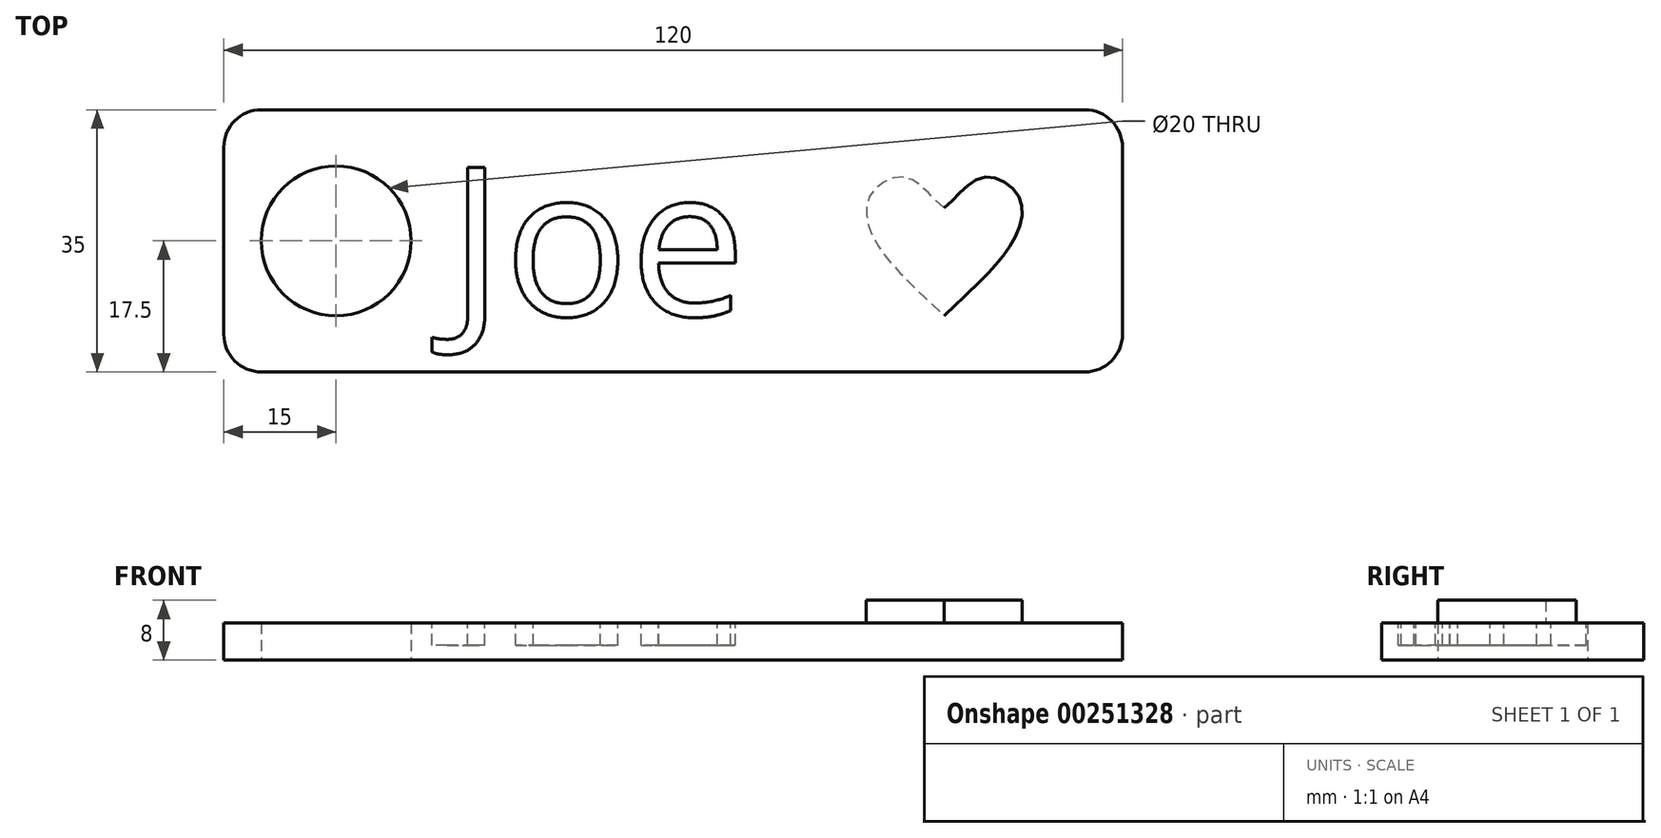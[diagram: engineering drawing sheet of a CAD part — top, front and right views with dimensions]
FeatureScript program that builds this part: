
annotation { "Feature Type Name" : "Feature", "Feature Type Description" : "" }
export const myFeature = defineFeature(function(context is Context, id is Id, definition is map)
    precondition{}
    {
        {
            var Q0;
            Q0=qCreatedBy(makeId("Top.planeOp"),FACE);
            var sketch = newSketch(context, id + "F0", { "sketchPlane" : qUnion([Q0])});
            skLineSegment(sketch, "E0.bottom", {"start": v(-60, 17.5) * mm, "end": v(60, 17.5) * mm});
            skLineSegment(sketch, "E0.top", {"start": v(-60, -17.5) * mm, "end": v(60, -17.5) * mm});
            skLineSegment(sketch, "E0.left", {"start": v(-60, 17.5) * mm, "end": v(-60, -17.5) * mm});
            skLineSegment(sketch, "E0.right", {"start": v(60, 17.5) * mm, "end": v(60, -17.5) * mm});
            skPoint(sketch, "E0.middle", {"position": v(0, 0) * mm});
            skCircle(sketch, "E1", {"center": v(-45, 0) * mm, "radius": 10 * mm});
            skSolve(sketch);
        }
        {
            var Q0;
            Q0=makeQuery(id+"F0.imprint","IMPRINT",FACE,{"disambiguationData":[TD([[makeQuery(id+"F0.imprint","IMPRINT",EDGE,{"derivedFrom":sQuery(id+"F0.wireOp",EDGE,"E0.bottom")}),-1.0]])]});
            extrude(context, id + "F1", {"entities" : qUnion([Q0]), "depth" : 5 * mm});
        }
        {
            var Q0;
            Q0=makeQuery(id+"F1.opExtrude","SWEPT_EDGE",EDGE,{"disambiguationData":[OSD([sQuery(id+"F0.wireOp",EDGE,"E0.top"),sQuery(id+"F0.wireOp",EDGE,"E0.left")])]});
            var Q1;
            Q1=makeQuery(id+"F1.opExtrude","SWEPT_EDGE",EDGE,{"disambiguationData":[OSD([sQuery(id+"F0.wireOp",EDGE,"E0.top"),sQuery(id+"F0.wireOp",EDGE,"E0.right")])]});
            var Q2;
            Q2=makeQuery(id+"F1.opExtrude","SWEPT_EDGE",EDGE,{"disambiguationData":[OSD([sQuery(id+"F0.wireOp",EDGE,"E0.bottom"),sQuery(id+"F0.wireOp",EDGE,"E0.right")])]});
            var Q3;
            Q3=makeQuery(id+"F1.opExtrude","SWEPT_EDGE",EDGE,{"disambiguationData":[OSD([sQuery(id+"F0.wireOp",EDGE,"E0.bottom"),sQuery(id+"F0.wireOp",EDGE,"E0.left")])]});
            fillet(context, id + "F2", {"entities" : qUnion([Q0, Q1, Q2, Q3]), "radius" : 5 * mm, "tangentPropagation" : true, "allowEdgeOverflow" : false});
        }
        {
            var Q0;
            Q0=makeQuery(id+"F1.opExtrude","CAP_FACE",FACE,{"disambiguationData":[OSD([sQuery(id+"F0.wireOp",EDGE,"E0.bottom"),sQuery(id+"F0.wireOp",EDGE,"E0.top"),sQuery(id+"F0.wireOp",EDGE,"E0.left"),sQuery(id+"F0.wireOp",EDGE,"E0.right"),sQuery(id+"F0.wireOp",EDGE,"E1")])],"isStart":false});
            var sketch = newSketch(context, id + "F3", { "sketchPlane" : qUnion([Q0])});
            skLineSegment(sketch, "E2", {"start": v(-44.38, 9.98) * mm, "end": v(60, 9.98) * mm, "construction": true});
            skLineSegment(sketch, "E3", {"start": v(-45.25, -10) * mm, "end": v(60, -10) * mm, "construction": true});
            skLineSegment(sketch, "E4", {"start": v(36.2, -10) * mm, "end": v(36.2, 9.98) * mm, "construction": true});
            skFitSpline(sketch, "E5", {"points": [v(36.2, 4.44) * mm, v(31.15, 8.44) * mm, v(26.28, 6) * mm, v(26.97, 0) * mm, v(31.5, -5.48) * mm, v(36.2, -10) * mm], "startDerivative": vector(-25.3, 18.56) * mm, "endDerivative": vector(41.06, -38.36) * mm});
            skFitSpline(sketch, "E6.MirrorCS", {"points": [v(36.2, 4.44) * mm, v(41.24, 8.44) * mm, v(46.12, 6) * mm, v(45.42, 0) * mm, v(40.9, -5.48) * mm, v(36.2, -10) * mm], "startDerivative": vector(25.3, 18.56) * mm, "endDerivative": vector(-41.06, -38.36) * mm});
            skText(sketch, "E7", { "text": "Joe", "fontName": "OpenSans-Regular.ttf"});
            const initialGuessF3  = {"E7": [-0.03, -0.01, 1, 0, 0.01998]};
            skSetInitialGuess(sketch, initialGuessF3);
            skSolve(sketch);
        }
        {
            var Q0;
            Q0=makeQuery(id+"F3.imprint","IMPRINT",FACE,{"disambiguationData":[TD([[makeQuery(id+"F3.imprint","IMPRINT",EDGE,{"derivedFrom":sQuery(id+"F3.wireOp",EDGE,"E5")}),1.0]])]});
            extrude(context, id + "F4", {"entities" : qUnion([Q0]), "operationType" : NewBodyOperationType.ADD, "depth" : 3 * mm});
        }
        {
            var Q0;
            Q0=makeQuery(id+"F3.imprint","IMPRINT",FACE,{"disambiguationData":[TD([[makeQuery(id+"F3.imprint","IMPRINT",EDGE,{"derivedFrom":sQuery(id+"F3.wireOp",EDGE,"E7.sketch_text.stroke-0")}),-1.0]])]});
            var Q1;
            Q1=makeQuery(id+"F3.imprint","IMPRINT",FACE,{"disambiguationData":[TD([[makeQuery(id+"F3.imprint","IMPRINT",EDGE,{"derivedFrom":sQuery(id+"F3.wireOp",EDGE,"E7.sketch_text.stroke-10")}),-1.0]])]});
            var Q2;
            Q2=makeQuery(id+"F3.imprint","IMPRINT",FACE,{"disambiguationData":[TD([[makeQuery(id+"F3.imprint","IMPRINT",EDGE,{"derivedFrom":sQuery(id+"F3.wireOp",EDGE,"E7.sketch_text.stroke-27")}),-1.0]])]});
            extrude(context, id + "F5", {"entities" : qUnion([Q0, Q1, Q2]), "operationType" : NewBodyOperationType.REMOVE, "oppositeDirection" : true, "depth" : 3 * mm});
        }
    });
